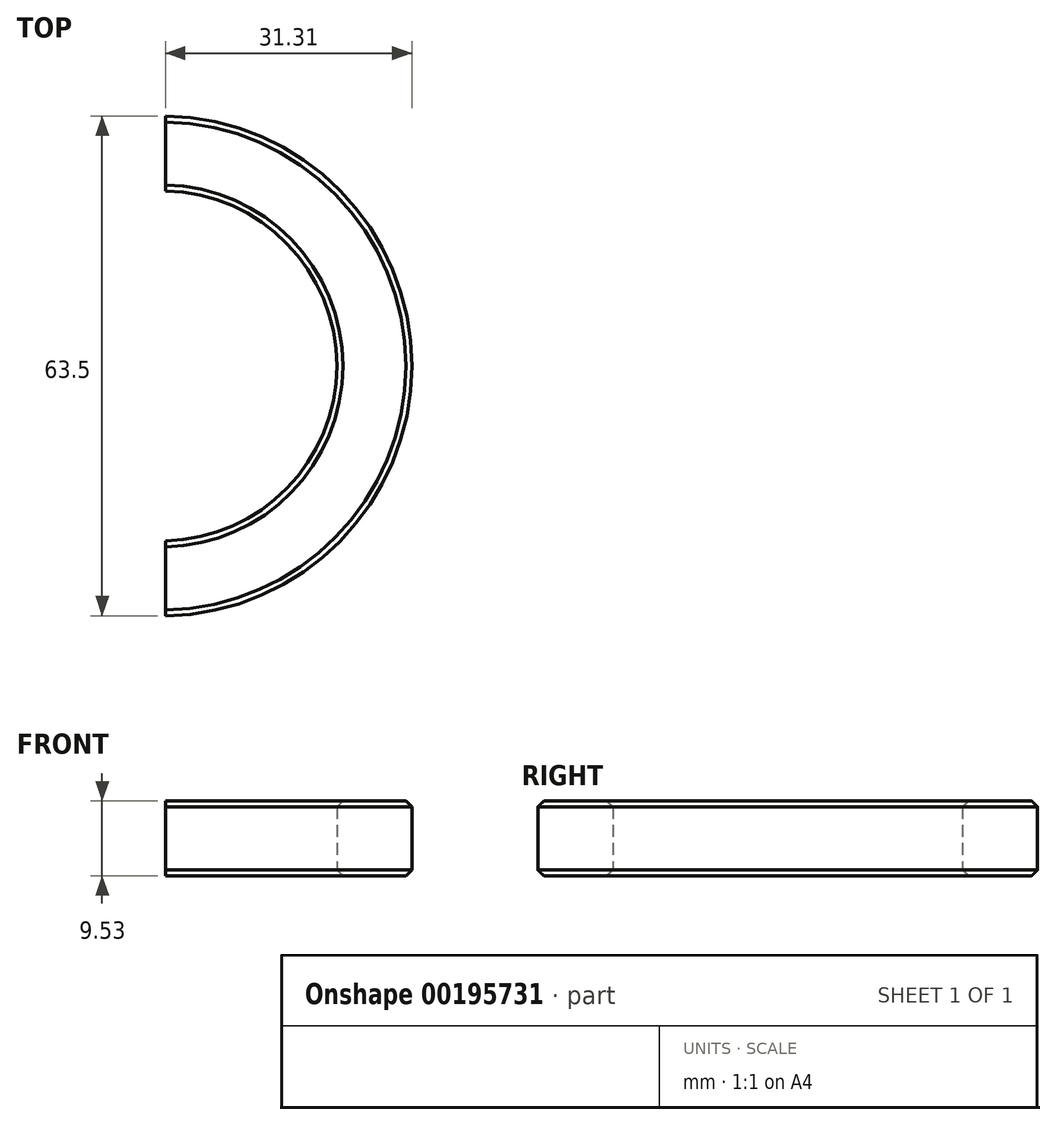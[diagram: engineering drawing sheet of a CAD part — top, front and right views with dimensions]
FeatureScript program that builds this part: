
annotation { "Feature Type Name" : "Feature", "Feature Type Description" : "" }
export const myFeature = defineFeature(function(context is Context, id is Id, definition is map)
    precondition{}
    {
        {
            var Q0;
            Q0=qCreatedBy(makeId("Top.planeOp"),FACE);
            var sketch = newSketch(context, id + "F0", { "sketchPlane" : qUnion([Q0])});
            skArc(sketch, "E0", {"start": v(0.44, -22.22) * mm, "mid": v(22.22, 0) * mm, "end": v(0.44, 22.22) * mm});
            skArc(sketch, "E1", {"start": v(0.44, -31.75) * mm, "mid": v(31.75, 0) * mm, "end": v(0.44, 31.75) * mm});
            skLineSegment(sketch, "E2", {"start": v(0.44, -31.75) * mm, "end": v(0.44, -22.22) * mm});
            skLineSegment(sketch, "E3.trimOffspring", {"start": v(0.44, 22.22) * mm, "end": v(0.44, 31.75) * mm});
            skSolve(sketch);
        }
        {
            var Q0;
            Q0 = qSketchRegion(id + "F0", true);
            extrude(context, id + "F1", {"entities" : qUnion([Q0]), "depth" : 9.52 * mm, "offsetDistance" : 25.4 * mm});
        }
        {
            var Q0;
            Q0=makeQuery(id+"F1.opExtrude","CAP_EDGE",EDGE,{"disambiguationData":[OSD([sQuery(id+"F0.wireOp",EDGE,"E1")])],"isStart":false});
            var Q1;
            Q1=makeQuery(id+"F1.opExtrude","CAP_EDGE",EDGE,{"disambiguationData":[OSD([sQuery(id+"F0.wireOp",EDGE,"E1")])],"isStart":true});
            var Q2;
            Q2=makeQuery(id+"F1.opExtrude","CAP_EDGE",EDGE,{"disambiguationData":[OSD([sQuery(id+"F0.wireOp",EDGE,"E0")])],"isStart":false});
            var Q3;
            Q3=makeQuery(id+"F1.opExtrude","CAP_EDGE",EDGE,{"disambiguationData":[OSD([sQuery(id+"F0.wireOp",EDGE,"E0")])],"isStart":true});
            chamfer(context, id + "F2", {"entities" : qUnion([Q0, Q1, Q2, Q3]), "width" : 0.76 * mm, "tangentPropagation" : true});
        }
    });
